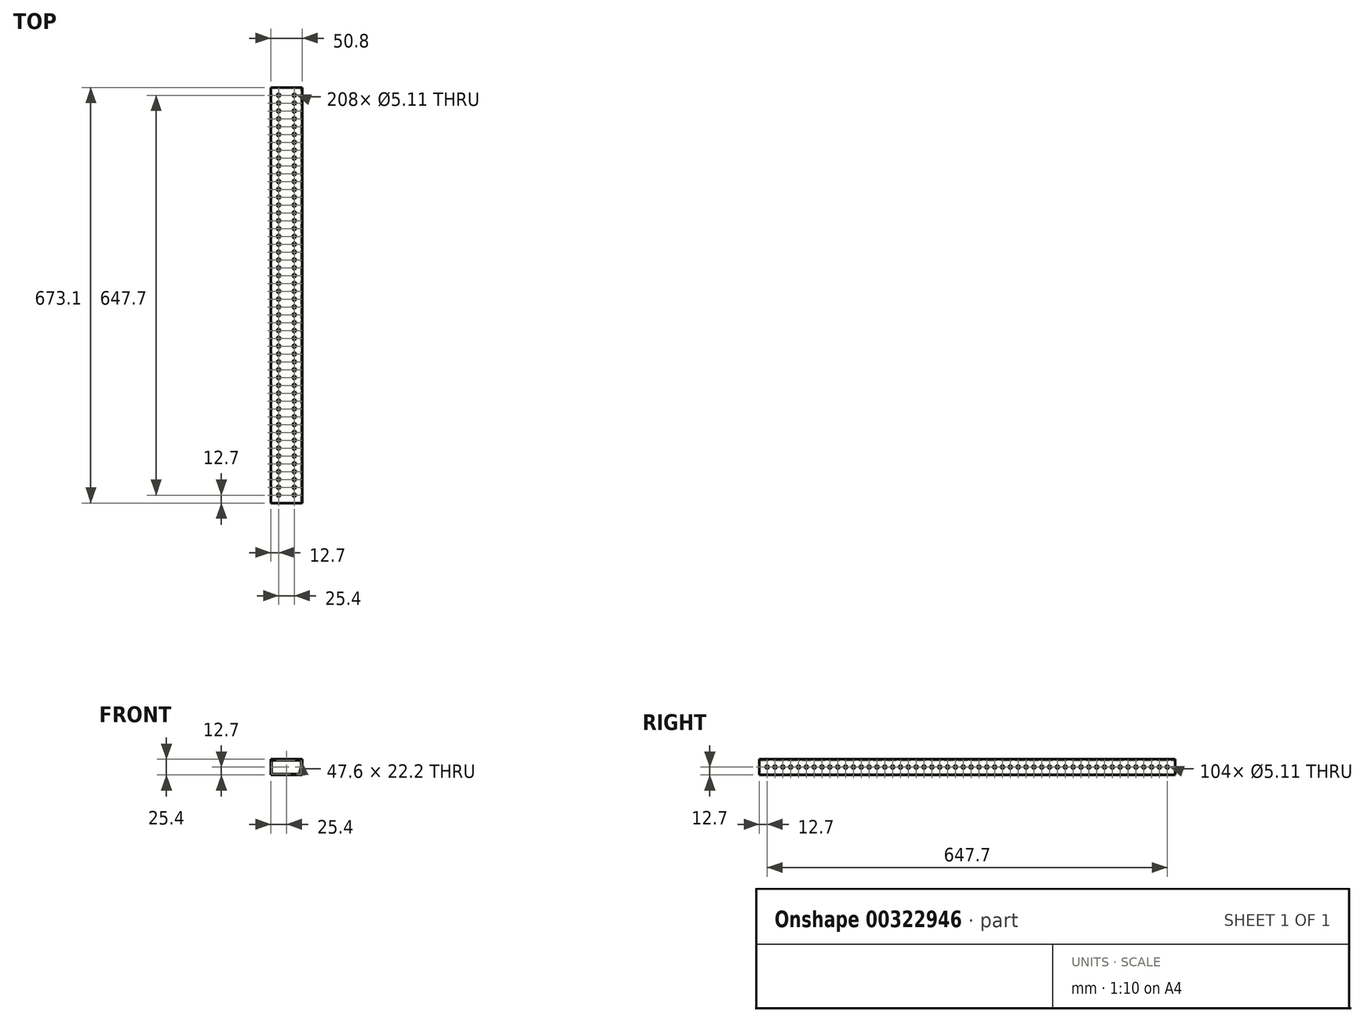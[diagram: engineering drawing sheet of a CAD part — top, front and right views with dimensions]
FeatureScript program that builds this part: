
annotation { "Feature Type Name" : "Feature", "Feature Type Description" : "" }
export const myFeature = defineFeature(function(context is Context, id is Id, definition is map)
    precondition{}
    {
        {
            var Q0;
            Q0=qCreatedBy(makeId("Front.planeOp"),FACE);
            var sketch = newSketch(context, id + "F0", { "sketchPlane" : qUnion([Q0])});
            skLineSegment(sketch, "E0.bottom", {"start": v(-25.4, 12.7) * mm, "end": v(25.4, 12.7) * mm});
            skLineSegment(sketch, "E0.top", {"start": v(-25.4, -12.7) * mm, "end": v(25.4, -12.7) * mm});
            skLineSegment(sketch, "E0.left", {"start": v(-25.4, 12.7) * mm, "end": v(-25.4, -12.7) * mm});
            skLineSegment(sketch, "E0.right", {"start": v(25.4, 12.7) * mm, "end": v(25.4, -12.7) * mm});
            skPoint(sketch, "E0.middle", {"position": v(0, 0) * mm});
            skLineSegment(sketch, "E1.bottom", {"start": v(-23.8, 11.1) * mm, "end": v(23.8, 11.1) * mm});
            skLineSegment(sketch, "E1.top", {"start": v(-23.8, -11.1) * mm, "end": v(23.8, -11.1) * mm});
            skLineSegment(sketch, "E1.left", {"start": v(-23.8, 11.1) * mm, "end": v(-23.8, -11.1) * mm});
            skLineSegment(sketch, "E1.right", {"start": v(23.8, 11.1) * mm, "end": v(23.8, -11.1) * mm});
            skSolve(sketch);
        }
        {
            var Q0;
            Q0=makeQuery(id+"F0.imprint","IMPRINT",FACE,{"disambiguationData":[TD([[makeQuery(id+"F0.imprint","IMPRINT",EDGE,{"derivedFrom":sQuery(id+"F0.wireOp",EDGE,"E0.bottom")}),-1.0]])]});
            extrude(context, id + "F1", {"entities" : qUnion([Q0]), "depth" : 673.1 * mm});
        }
        {
            var Q0;
            Q0=makeQuery(id+"F1.opExtrude","SWEPT_FACE",FACE,{"disambiguationData":[OSD([sQuery(id+"F0.wireOp",EDGE,"E0.bottom")])]});
            var sketch = newSketch(context, id + "F2", { "sketchPlane" : qUnion([Q0])});
            skCircle(sketch, "E2", {"center": v(-12.7, -660.4) * mm, "radius": 2.55 * mm});
            skCircle(sketch, "E3.0.1.0", {"center": v(-12.7, -647.7) * mm, "radius": 2.55 * mm});
            skCircle(sketch, "E3.0.2.0", {"center": v(-12.7, -635) * mm, "radius": 2.55 * mm});
            skCircle(sketch, "E3.0.3.0", {"center": v(-12.7, -622.3) * mm, "radius": 2.55 * mm});
            skCircle(sketch, "E3.0.4.0", {"center": v(-12.7, -609.6) * mm, "radius": 2.55 * mm});
            skCircle(sketch, "E3.0.5.0", {"center": v(-12.7, -596.9) * mm, "radius": 2.55 * mm});
            skCircle(sketch, "E3.0.6.0", {"center": v(-12.7, -584.2) * mm, "radius": 2.55 * mm});
            skCircle(sketch, "E3.0.7.0", {"center": v(-12.7, -571.5) * mm, "radius": 2.55 * mm});
            skCircle(sketch, "E3.0.8.0", {"center": v(-12.7, -558.8) * mm, "radius": 2.55 * mm});
            skCircle(sketch, "E3.0.9.0", {"center": v(-12.7, -546.1) * mm, "radius": 2.55 * mm});
            skCircle(sketch, "E3.0.10.0", {"center": v(-12.7, -533.4) * mm, "radius": 2.55 * mm});
            skCircle(sketch, "E3.0.11.0", {"center": v(-12.7, -520.7) * mm, "radius": 2.55 * mm});
            skCircle(sketch, "E3.0.12.0", {"center": v(-12.7, -508) * mm, "radius": 2.55 * mm});
            skCircle(sketch, "E3.0.13.0", {"center": v(-12.7, -495.3) * mm, "radius": 2.55 * mm});
            skCircle(sketch, "E3.0.14.0", {"center": v(-12.7, -482.6) * mm, "radius": 2.55 * mm});
            skCircle(sketch, "E3.0.15.0", {"center": v(-12.7, -469.9) * mm, "radius": 2.55 * mm});
            skCircle(sketch, "E3.0.16.0", {"center": v(-12.7, -457.2) * mm, "radius": 2.55 * mm});
            skCircle(sketch, "E3.0.17.0", {"center": v(-12.7, -444.5) * mm, "radius": 2.55 * mm});
            skCircle(sketch, "E3.0.18.0", {"center": v(-12.7, -431.8) * mm, "radius": 2.55 * mm});
            skCircle(sketch, "E3.0.19.0", {"center": v(-12.7, -419.1) * mm, "radius": 2.55 * mm});
            skCircle(sketch, "E3.0.20.0", {"center": v(-12.7, -406.4) * mm, "radius": 2.55 * mm});
            skCircle(sketch, "E3.0.21.0", {"center": v(-12.7, -393.7) * mm, "radius": 2.55 * mm});
            skCircle(sketch, "E3.0.22.0", {"center": v(-12.7, -381) * mm, "radius": 2.55 * mm});
            skCircle(sketch, "E3.0.23.0", {"center": v(-12.7, -368.3) * mm, "radius": 2.55 * mm});
            skCircle(sketch, "E3.0.24.0", {"center": v(-12.7, -355.6) * mm, "radius": 2.55 * mm});
            skCircle(sketch, "E3.0.25.0", {"center": v(-12.7, -342.9) * mm, "radius": 2.55 * mm});
            skCircle(sketch, "E3.1.0.0", {"center": v(12.7, -660.4) * mm, "radius": 2.55 * mm});
            skCircle(sketch, "E3.1.1.0", {"center": v(12.7, -647.7) * mm, "radius": 2.55 * mm});
            skCircle(sketch, "E3.1.2.0", {"center": v(12.7, -635) * mm, "radius": 2.55 * mm});
            skCircle(sketch, "E3.1.3.0", {"center": v(12.7, -622.3) * mm, "radius": 2.55 * mm});
            skCircle(sketch, "E3.1.4.0", {"center": v(12.7, -609.6) * mm, "radius": 2.55 * mm});
            skCircle(sketch, "E3.1.5.0", {"center": v(12.7, -596.9) * mm, "radius": 2.55 * mm});
            skCircle(sketch, "E3.1.6.0", {"center": v(12.7, -584.2) * mm, "radius": 2.55 * mm});
            skCircle(sketch, "E3.1.7.0", {"center": v(12.7, -571.5) * mm, "radius": 2.55 * mm});
            skCircle(sketch, "E3.1.8.0", {"center": v(12.7, -558.8) * mm, "radius": 2.55 * mm});
            skCircle(sketch, "E3.1.9.0", {"center": v(12.7, -546.1) * mm, "radius": 2.55 * mm});
            skCircle(sketch, "E3.1.10.0", {"center": v(12.7, -533.4) * mm, "radius": 2.55 * mm});
            skCircle(sketch, "E3.1.11.0", {"center": v(12.7, -520.7) * mm, "radius": 2.55 * mm});
            skCircle(sketch, "E3.1.12.0", {"center": v(12.7, -508) * mm, "radius": 2.55 * mm});
            skCircle(sketch, "E3.1.13.0", {"center": v(12.7, -495.3) * mm, "radius": 2.55 * mm});
            skCircle(sketch, "E3.1.14.0", {"center": v(12.7, -482.6) * mm, "radius": 2.55 * mm});
            skCircle(sketch, "E3.1.15.0", {"center": v(12.7, -469.9) * mm, "radius": 2.55 * mm});
            skCircle(sketch, "E3.1.16.0", {"center": v(12.7, -457.2) * mm, "radius": 2.55 * mm});
            skCircle(sketch, "E3.1.17.0", {"center": v(12.7, -444.5) * mm, "radius": 2.55 * mm});
            skCircle(sketch, "E3.1.18.0", {"center": v(12.7, -431.8) * mm, "radius": 2.55 * mm});
            skCircle(sketch, "E3.1.19.0", {"center": v(12.7, -419.1) * mm, "radius": 2.55 * mm});
            skCircle(sketch, "E3.1.20.0", {"center": v(12.7, -406.4) * mm, "radius": 2.55 * mm});
            skCircle(sketch, "E3.1.21.0", {"center": v(12.7, -393.7) * mm, "radius": 2.55 * mm});
            skCircle(sketch, "E3.1.22.0", {"center": v(12.7, -381) * mm, "radius": 2.55 * mm});
            skCircle(sketch, "E3.1.23.0", {"center": v(12.7, -368.3) * mm, "radius": 2.55 * mm});
            skCircle(sketch, "E3.1.24.0", {"center": v(12.7, -355.6) * mm, "radius": 2.55 * mm});
            skCircle(sketch, "E3.1.25.0", {"center": v(12.7, -342.9) * mm, "radius": 2.55 * mm});
            skLineSegment(sketch, "E3.direction1", {"start": v(-12.7, -660.4) * mm, "end": v(12.7, -660.4) * mm, "construction": true});
            skLineSegment(sketch, "E3.direction2", {"start": v(-12.7, -660.4) * mm, "end": v(-12.7, -647.7) * mm, "construction": true});
            skCircle(sketch, "E4.0.0.26", {"center": v(-12.7, -330.2) * mm, "radius": 2.55 * mm});
            skCircle(sketch, "E4.0.0.27", {"center": v(-12.7, -317.5) * mm, "radius": 2.55 * mm});
            skCircle(sketch, "E4.0.0.28", {"center": v(-12.7, -304.8) * mm, "radius": 2.55 * mm});
            skCircle(sketch, "E4.0.0.29", {"center": v(-12.7, -292.1) * mm, "radius": 2.55 * mm});
            skCircle(sketch, "E4.0.0.30", {"center": v(-12.7, -279.4) * mm, "radius": 2.55 * mm});
            skCircle(sketch, "E4.0.0.31", {"center": v(-12.7, -266.7) * mm, "radius": 2.55 * mm});
            skCircle(sketch, "E4.0.0.32", {"center": v(-12.7, -254) * mm, "radius": 2.55 * mm});
            skCircle(sketch, "E4.0.0.33", {"center": v(-12.7, -241.3) * mm, "radius": 2.55 * mm});
            skCircle(sketch, "E4.0.0.34", {"center": v(-12.7, -228.6) * mm, "radius": 2.55 * mm});
            skCircle(sketch, "E4.0.0.35", {"center": v(-12.7, -215.9) * mm, "radius": 2.55 * mm});
            skCircle(sketch, "E4.0.0.36", {"center": v(-12.7, -203.2) * mm, "radius": 2.55 * mm});
            skCircle(sketch, "E4.0.0.37", {"center": v(-12.7, -190.5) * mm, "radius": 2.55 * mm});
            skCircle(sketch, "E4.0.0.38", {"center": v(-12.7, -177.8) * mm, "radius": 2.55 * mm});
            skCircle(sketch, "E4.0.0.39", {"center": v(-12.7, -165.1) * mm, "radius": 2.55 * mm});
            skCircle(sketch, "E4.0.0.40", {"center": v(-12.7, -152.4) * mm, "radius": 2.55 * mm});
            skCircle(sketch, "E4.0.0.41", {"center": v(-12.7, -139.7) * mm, "radius": 2.55 * mm});
            skCircle(sketch, "E4.0.0.42", {"center": v(-12.7, -127) * mm, "radius": 2.55 * mm});
            skCircle(sketch, "E4.0.0.43", {"center": v(-12.7, -114.3) * mm, "radius": 2.55 * mm});
            skCircle(sketch, "E4.0.0.44", {"center": v(-12.7, -101.6) * mm, "radius": 2.55 * mm});
            skCircle(sketch, "E4.0.0.45", {"center": v(-12.7, -88.9) * mm, "radius": 2.55 * mm});
            skCircle(sketch, "E4.0.1.26", {"center": v(12.7, -330.2) * mm, "radius": 2.55 * mm});
            skCircle(sketch, "E4.0.1.27", {"center": v(12.7, -317.5) * mm, "radius": 2.55 * mm});
            skCircle(sketch, "E4.0.1.28", {"center": v(12.7, -304.8) * mm, "radius": 2.55 * mm});
            skCircle(sketch, "E4.0.1.29", {"center": v(12.7, -292.1) * mm, "radius": 2.55 * mm});
            skCircle(sketch, "E4.0.1.30", {"center": v(12.7, -279.4) * mm, "radius": 2.55 * mm});
            skCircle(sketch, "E4.0.1.31", {"center": v(12.7, -266.7) * mm, "radius": 2.55 * mm});
            skCircle(sketch, "E4.0.1.32", {"center": v(12.7, -254) * mm, "radius": 2.55 * mm});
            skCircle(sketch, "E4.0.1.33", {"center": v(12.7, -241.3) * mm, "radius": 2.55 * mm});
            skCircle(sketch, "E4.0.1.34", {"center": v(12.7, -228.6) * mm, "radius": 2.55 * mm});
            skCircle(sketch, "E4.0.1.35", {"center": v(12.7, -215.9) * mm, "radius": 2.55 * mm});
            skCircle(sketch, "E4.0.1.36", {"center": v(12.7, -203.2) * mm, "radius": 2.55 * mm});
            skCircle(sketch, "E4.0.1.37", {"center": v(12.7, -190.5) * mm, "radius": 2.55 * mm});
            skCircle(sketch, "E4.0.1.38", {"center": v(12.7, -177.8) * mm, "radius": 2.55 * mm});
            skCircle(sketch, "E4.0.1.39", {"center": v(12.7, -165.1) * mm, "radius": 2.55 * mm});
            skCircle(sketch, "E4.0.1.40", {"center": v(12.7, -152.4) * mm, "radius": 2.55 * mm});
            skCircle(sketch, "E4.0.1.41", {"center": v(12.7, -139.7) * mm, "radius": 2.55 * mm});
            skCircle(sketch, "E4.0.1.42", {"center": v(12.7, -127) * mm, "radius": 2.55 * mm});
            skCircle(sketch, "E4.0.1.43", {"center": v(12.7, -114.3) * mm, "radius": 2.55 * mm});
            skCircle(sketch, "E4.0.1.44", {"center": v(12.7, -101.6) * mm, "radius": 2.55 * mm});
            skCircle(sketch, "E4.0.1.45", {"center": v(12.7, -88.9) * mm, "radius": 2.55 * mm});
            skCircle(sketch, "E5.0.0.46", {"center": v(-12.7, -76.2) * mm, "radius": 2.55 * mm});
            skCircle(sketch, "E5.0.0.47", {"center": v(-12.7, -63.5) * mm, "radius": 2.55 * mm});
            skCircle(sketch, "E5.0.0.48", {"center": v(-12.7, -50.8) * mm, "radius": 2.55 * mm});
            skCircle(sketch, "E5.0.0.49", {"center": v(-12.7, -38.1) * mm, "radius": 2.55 * mm});
            skCircle(sketch, "E5.0.1.46", {"center": v(12.7, -76.2) * mm, "radius": 2.55 * mm});
            skCircle(sketch, "E5.0.1.47", {"center": v(12.7, -63.5) * mm, "radius": 2.55 * mm});
            skCircle(sketch, "E5.0.1.48", {"center": v(12.7, -50.8) * mm, "radius": 2.55 * mm});
            skCircle(sketch, "E5.0.1.49", {"center": v(12.7, -38.1) * mm, "radius": 2.55 * mm});
            skCircle(sketch, "E6.0.0.50", {"center": v(-12.7, -25.4) * mm, "radius": 2.55 * mm});
            skCircle(sketch, "E6.0.1.50", {"center": v(12.7, -25.4) * mm, "radius": 2.55 * mm});
            skCircle(sketch, "E7.0.0.51", {"center": v(-12.7, -12.7) * mm, "radius": 2.55 * mm});
            skCircle(sketch, "E7.0.1.51", {"center": v(12.7, -12.7) * mm, "radius": 2.55 * mm});
            skSolve(sketch);
        }
        {
            var Q0;
            Q0=makeQuery(id+"F1.opExtrude","SWEPT_FACE",FACE,{"disambiguationData":[OSD([sQuery(id+"F0.wireOp",EDGE,"E0.right")])]});
            var sketch = newSketch(context, id + "F3", { "sketchPlane" : qUnion([Q0])});
            skCircle(sketch, "E8", {"center": v(-660.4, 0) * mm, "radius": 2.55 * mm});
            skCircle(sketch, "E9.1.0.0", {"center": v(-647.7, 0) * mm, "radius": 2.55 * mm});
            skCircle(sketch, "E9.2.0.0", {"center": v(-635, 0) * mm, "radius": 2.55 * mm});
            skCircle(sketch, "E9.3.0.0", {"center": v(-622.3, 0) * mm, "radius": 2.55 * mm});
            skCircle(sketch, "E9.4.0.0", {"center": v(-609.6, 0) * mm, "radius": 2.55 * mm});
            skCircle(sketch, "E9.5.0.0", {"center": v(-596.9, 0) * mm, "radius": 2.55 * mm});
            skCircle(sketch, "E9.6.0.0", {"center": v(-584.2, 0) * mm, "radius": 2.55 * mm});
            skCircle(sketch, "E9.7.0.0", {"center": v(-571.5, 0) * mm, "radius": 2.55 * mm});
            skCircle(sketch, "E9.8.0.0", {"center": v(-558.8, 0) * mm, "radius": 2.55 * mm});
            skCircle(sketch, "E9.9.0.0", {"center": v(-546.1, 0) * mm, "radius": 2.55 * mm});
            skCircle(sketch, "E9.10.0.0", {"center": v(-533.4, 0) * mm, "radius": 2.55 * mm});
            skCircle(sketch, "E9.11.0.0", {"center": v(-520.7, 0) * mm, "radius": 2.55 * mm});
            skCircle(sketch, "E9.12.0.0", {"center": v(-508, 0) * mm, "radius": 2.55 * mm});
            skCircle(sketch, "E9.13.0.0", {"center": v(-495.3, 0) * mm, "radius": 2.55 * mm});
            skCircle(sketch, "E9.14.0.0", {"center": v(-482.6, 0) * mm, "radius": 2.55 * mm});
            skCircle(sketch, "E9.15.0.0", {"center": v(-469.9, 0) * mm, "radius": 2.55 * mm});
            skCircle(sketch, "E9.16.0.0", {"center": v(-457.2, 0) * mm, "radius": 2.55 * mm});
            skCircle(sketch, "E9.17.0.0", {"center": v(-444.5, 0) * mm, "radius": 2.55 * mm});
            skCircle(sketch, "E9.18.0.0", {"center": v(-431.8, 0) * mm, "radius": 2.55 * mm});
            skCircle(sketch, "E9.19.0.0", {"center": v(-419.1, 0) * mm, "radius": 2.55 * mm});
            skCircle(sketch, "E9.20.0.0", {"center": v(-406.4, 0) * mm, "radius": 2.55 * mm});
            skCircle(sketch, "E9.21.0.0", {"center": v(-393.7, 0) * mm, "radius": 2.55 * mm});
            skCircle(sketch, "E9.22.0.0", {"center": v(-381, 0) * mm, "radius": 2.55 * mm});
            skCircle(sketch, "E9.23.0.0", {"center": v(-368.3, 0) * mm, "radius": 2.55 * mm});
            skCircle(sketch, "E9.24.0.0", {"center": v(-355.6, 0) * mm, "radius": 2.55 * mm});
            skCircle(sketch, "E9.25.0.0", {"center": v(-342.9, 0) * mm, "radius": 2.55 * mm});
            skLineSegment(sketch, "E9.direction1", {"start": v(-660.4, 0) * mm, "end": v(-647.7, 0) * mm, "construction": true});
            skCircle(sketch, "E10.0.26.0", {"center": v(-330.2, 0) * mm, "radius": 2.55 * mm});
            skCircle(sketch, "E10.0.27.0", {"center": v(-317.5, 0) * mm, "radius": 2.55 * mm});
            skCircle(sketch, "E10.0.28.0", {"center": v(-304.8, 0) * mm, "radius": 2.55 * mm});
            skCircle(sketch, "E10.0.29.0", {"center": v(-292.1, 0) * mm, "radius": 2.55 * mm});
            skCircle(sketch, "E10.0.30.0", {"center": v(-279.4, 0) * mm, "radius": 2.55 * mm});
            skCircle(sketch, "E10.0.31.0", {"center": v(-266.7, 0) * mm, "radius": 2.55 * mm});
            skCircle(sketch, "E10.0.32.0", {"center": v(-254, 0) * mm, "radius": 2.55 * mm});
            skCircle(sketch, "E10.0.33.0", {"center": v(-241.3, 0) * mm, "radius": 2.55 * mm});
            skCircle(sketch, "E10.0.34.0", {"center": v(-228.6, 0) * mm, "radius": 2.55 * mm});
            skCircle(sketch, "E10.0.35.0", {"center": v(-215.9, 0) * mm, "radius": 2.55 * mm});
            skCircle(sketch, "E10.0.36.0", {"center": v(-203.2, 0) * mm, "radius": 2.55 * mm});
            skCircle(sketch, "E10.0.37.0", {"center": v(-190.5, 0) * mm, "radius": 2.55 * mm});
            skCircle(sketch, "E10.0.38.0", {"center": v(-177.8, 0) * mm, "radius": 2.55 * mm});
            skCircle(sketch, "E10.0.39.0", {"center": v(-165.1, 0) * mm, "radius": 2.55 * mm});
            skCircle(sketch, "E10.0.40.0", {"center": v(-152.4, 0) * mm, "radius": 2.55 * mm});
            skCircle(sketch, "E10.0.41.0", {"center": v(-139.7, 0) * mm, "radius": 2.55 * mm});
            skCircle(sketch, "E10.0.42.0", {"center": v(-127, 0) * mm, "radius": 2.55 * mm});
            skCircle(sketch, "E10.0.43.0", {"center": v(-114.3, 0) * mm, "radius": 2.55 * mm});
            skCircle(sketch, "E10.0.44.0", {"center": v(-101.6, 0) * mm, "radius": 2.55 * mm});
            skCircle(sketch, "E10.0.45.0", {"center": v(-88.9, 0) * mm, "radius": 2.55 * mm});
            skCircle(sketch, "E10.0.46.0", {"center": v(-76.2, 0) * mm, "radius": 2.55 * mm});
            skCircle(sketch, "E10.0.47.0", {"center": v(-63.5, 0) * mm, "radius": 2.55 * mm});
            skCircle(sketch, "E10.0.48.0", {"center": v(-50.8, 0) * mm, "radius": 2.55 * mm});
            skCircle(sketch, "E10.0.49.0", {"center": v(-38.1, 0) * mm, "radius": 2.55 * mm});
            skCircle(sketch, "E10.0.50.0", {"center": v(-25.4, 0) * mm, "radius": 2.55 * mm});
            skCircle(sketch, "E10.0.51.0", {"center": v(-12.7, 0) * mm, "radius": 2.55 * mm});
            skSolve(sketch);
        }
        {
            var Q0;
            Q0=sQuery(id+"F3.wireOp",VERTEX,"E9.25.0.0.center");
            var Q1;
            Q1=sQuery(id+"F3.wireOp",VERTEX,"E9.23.0.0.center");
            var Q2;
            Q2=sQuery(id+"F3.wireOp",VERTEX,"E9.16.0.0.center");
            var Q3;
            Q3=sQuery(id+"F3.wireOp",VERTEX,"E9.14.0.0.center");
            var Q4;
            Q4=sQuery(id+"F3.wireOp",VERTEX,"E9.20.0.0.center");
            var Q5;
            Q5=sQuery(id+"F3.wireOp",VERTEX,"E9.18.0.0.center");
            var Q6;
            Q6=sQuery(id+"F3.wireOp",VERTEX,"E8.center");
            var Q7;
            Q7=sQuery(id+"F3.wireOp",VERTEX,"E9.3.0.0.center");
            var Q8;
            Q8=sQuery(id+"F3.wireOp",VERTEX,"E9.2.0.0.center");
            var Q9;
            Q9=sQuery(id+"F3.wireOp",VERTEX,"E9.4.0.0.center");
            var Q10;
            Q10=sQuery(id+"F3.wireOp",VERTEX,"E9.5.0.0.center");
            var Q11;
            Q11=sQuery(id+"F3.wireOp",VERTEX,"E9.12.0.0.center");
            var Q12;
            Q12=sQuery(id+"F3.wireOp",VERTEX,"E9.11.0.0.center");
            var Q13;
            Q13=sQuery(id+"F3.wireOp",VERTEX,"E9.21.0.0.center");
            var Q14;
            Q14=sQuery(id+"F3.wireOp",VERTEX,"E9.13.0.0.center");
            var Q15;
            Q15=sQuery(id+"F3.wireOp",VERTEX,"E9.direction1.end");
            var Q16;
            Q16=sQuery(id+"F3.wireOp",VERTEX,"E9.24.0.0.center");
            var Q17;
            Q17=sQuery(id+"F3.wireOp",VERTEX,"E9.15.0.0.center");
            var Q18;
            Q18=sQuery(id+"F3.wireOp",VERTEX,"E9.7.0.0.center");
            var Q19;
            Q19=sQuery(id+"F3.wireOp",VERTEX,"E9.19.0.0.center");
            var Q20;
            Q20=sQuery(id+"F3.wireOp",VERTEX,"E9.6.0.0.center");
            var Q21;
            Q21=sQuery(id+"F3.wireOp",VERTEX,"E9.9.0.0.center");
            var Q22;
            Q22=sQuery(id+"F3.wireOp",VERTEX,"E9.17.0.0.center");
            var Q23;
            Q23=sQuery(id+"F3.wireOp",VERTEX,"E9.8.0.0.center");
            var Q24;
            Q24=sQuery(id+"F3.wireOp",VERTEX,"E9.10.0.0.center");
            var Q25;
            Q25=sQuery(id+"F3.wireOp",VERTEX,"E9.22.0.0.center");
            var Q26;
            Q26=sQuery(id+"F3.wireOp",VERTEX,"E10.0.48.0.center");
            var Q27;
            Q27=sQuery(id+"F3.wireOp",VERTEX,"E10.0.31.0.center");
            var Q28;
            Q28=sQuery(id+"F3.wireOp",VERTEX,"E10.0.32.0.center");
            var Q29;
            Q29=sQuery(id+"F3.wireOp",VERTEX,"E10.0.44.0.center");
            var Q30;
            Q30=sQuery(id+"F3.wireOp",VERTEX,"E10.0.36.0.center");
            var Q31;
            Q31=sQuery(id+"F3.wireOp",VERTEX,"E10.0.28.0.center");
            var Q32;
            Q32=sQuery(id+"F3.wireOp",VERTEX,"E10.0.27.0.center");
            var Q33;
            Q33=sQuery(id+"F3.wireOp",VERTEX,"E10.0.43.0.center");
            var Q34;
            Q34=sQuery(id+"F3.wireOp",VERTEX,"E10.0.51.0.center");
            var Q35;
            Q35=sQuery(id+"F3.wireOp",VERTEX,"E10.0.29.0.center");
            var Q36;
            Q36=sQuery(id+"F3.wireOp",VERTEX,"E10.0.33.0.center");
            var Q37;
            Q37=sQuery(id+"F3.wireOp",VERTEX,"E10.0.37.0.center");
            var Q38;
            Q38=sQuery(id+"F3.wireOp",VERTEX,"E10.0.49.0.center");
            var Q39;
            Q39=sQuery(id+"F3.wireOp",VERTEX,"E10.0.45.0.center");
            var Q40;
            Q40=sQuery(id+"F3.wireOp",VERTEX,"E10.0.39.0.center");
            var Q41;
            Q41=sQuery(id+"F3.wireOp",VERTEX,"E10.0.46.0.center");
            var Q42;
            Q42=sQuery(id+"F3.wireOp",VERTEX,"E10.0.30.0.center");
            var Q43;
            Q43=sQuery(id+"F3.wireOp",VERTEX,"E10.0.50.0.center");
            var Q44;
            Q44=sQuery(id+"F3.wireOp",VERTEX,"E10.0.40.0.center");
            var Q45;
            Q45=sQuery(id+"F3.wireOp",VERTEX,"E10.0.34.0.center");
            var Q46;
            Q46=sQuery(id+"F3.wireOp",VERTEX,"E10.0.35.0.center");
            var Q47;
            Q47=sQuery(id+"F3.wireOp",VERTEX,"E10.0.41.0.center");
            var Q48;
            Q48=sQuery(id+"F3.wireOp",VERTEX,"E10.0.38.0.center");
            var Q49;
            Q49=sQuery(id+"F3.wireOp",VERTEX,"E10.0.47.0.center");
            var Q50;
            Q50=sQuery(id+"F3.wireOp",VERTEX,"E10.0.42.0.center");
            var Q51;
            Q51=sQuery(id+"F3.wireOp",VERTEX,"E10.0.26.0.center");
            var Q52;
            Q52=makeQuery(id+"F1.opExtrude","SWEPT_BODY",BODY,{"disambiguationData":[OSD([sQuery(id+"F0.wireOp",EDGE,"E0.bottom"),sQuery(id+"F0.wireOp",EDGE,"E0.top"),sQuery(id+"F0.wireOp",EDGE,"E0.left"),sQuery(id+"F0.wireOp",EDGE,"E0.right"),sQuery(id+"F0.wireOp",EDGE,"E1.bottom"),sQuery(id+"F0.wireOp",EDGE,"E1.top"),sQuery(id+"F0.wireOp",EDGE,"E1.left"),sQuery(id+"F0.wireOp",EDGE,"E1.right")])]});
            hole(context, id + "F4", {"style" : HoleStyle.SIMPLE, "endStyle" : HoleEndStyle.THROUGH, "holeDiameter" : 5.1 * mm, "isTappedThrough" : true, "tappedDepth" : 12.7 * mm, "tapClearance" : 3, "locations" : qUnion([Q0, Q1, Q2, Q3, Q4, Q5, Q6, Q7, Q8, Q9, Q10, Q11, Q12, Q13, Q14, Q15, Q16, Q17, Q18, Q19, Q20, Q21, Q22, Q23, Q24, Q25, Q26, Q27, Q28, Q29, Q30, Q31, Q32, Q33, Q34, Q35, Q36, Q37, Q38, Q39, Q40, Q41, Q42, Q43, Q44, Q45, Q46, Q47, Q48, Q49, Q50, Q51]), "scope" : qUnion([Q52])});
        }
        {
            var Q0;
            Q0=sQuery(id+"F2.wireOp",VERTEX,"E4.0.0.39.center");
            var Q1;
            Q1=sQuery(id+"F2.wireOp",VERTEX,"E4.0.0.32.center");
            var Q2;
            Q2=sQuery(id+"F2.wireOp",VERTEX,"E3.0.23.0.center");
            var Q3;
            Q3=sQuery(id+"F2.wireOp",VERTEX,"E4.0.0.29.center");
            var Q4;
            Q4=sQuery(id+"F2.wireOp",VERTEX,"E3.1.22.0.center");
            var Q5;
            Q5=sQuery(id+"F2.wireOp",VERTEX,"E4.0.0.31.center");
            var Q6;
            Q6=sQuery(id+"F2.wireOp",VERTEX,"E3.1.23.0.center");
            var Q7;
            Q7=sQuery(id+"F2.wireOp",VERTEX,"E4.0.1.44.center");
            var Q8;
            Q8=sQuery(id+"F2.wireOp",VERTEX,"E5.0.1.46.center");
            var Q9;
            Q9=sQuery(id+"F2.wireOp",VERTEX,"E4.0.1.34.center");
            var Q10;
            Q10=sQuery(id+"F2.wireOp",VERTEX,"E4.0.0.44.center");
            var Q11;
            Q11=sQuery(id+"F2.wireOp",VERTEX,"E3.0.25.0.center");
            var Q12;
            Q12=sQuery(id+"F2.wireOp",VERTEX,"E4.0.1.43.center");
            var Q13;
            Q13=sQuery(id+"F2.wireOp",VERTEX,"E4.0.1.40.center");
            var Q14;
            Q14=sQuery(id+"F2.wireOp",VERTEX,"E4.0.1.35.center");
            var Q15;
            Q15=sQuery(id+"F2.wireOp",VERTEX,"E4.0.0.45.center");
            var Q16;
            Q16=sQuery(id+"F2.wireOp",VERTEX,"E4.0.1.41.center");
            var Q17;
            Q17=sQuery(id+"F2.wireOp",VERTEX,"E5.0.1.47.center");
            var Q18;
            Q18=sQuery(id+"F2.wireOp",VERTEX,"E4.0.0.38.center");
            var Q19;
            Q19=sQuery(id+"F2.wireOp",VERTEX,"E4.0.1.27.center");
            var Q20;
            Q20=sQuery(id+"F2.wireOp",VERTEX,"E4.0.1.28.center");
            var Q21;
            Q21=sQuery(id+"F2.wireOp",VERTEX,"E4.0.1.33.center");
            var Q22;
            Q22=sQuery(id+"F2.wireOp",VERTEX,"E4.0.1.32.center");
            var Q23;
            Q23=sQuery(id+"F2.wireOp",VERTEX,"E4.0.1.42.center");
            var Q24;
            Q24=sQuery(id+"F2.wireOp",VERTEX,"E5.0.0.46.center");
            var Q25;
            Q25=sQuery(id+"F2.wireOp",VERTEX,"E4.0.1.38.center");
            var Q26;
            Q26=sQuery(id+"F2.wireOp",VERTEX,"E4.0.1.29.center");
            var Q27;
            Q27=sQuery(id+"F2.wireOp",VERTEX,"E4.0.0.43.center");
            var Q28;
            Q28=sQuery(id+"F2.wireOp",VERTEX,"E4.0.1.39.center");
            var Q29;
            Q29=sQuery(id+"F2.wireOp",VERTEX,"E4.0.0.33.center");
            var Q30;
            Q30=sQuery(id+"F2.wireOp",VERTEX,"E4.0.0.27.center");
            var Q31;
            Q31=sQuery(id+"F2.wireOp",VERTEX,"E3.1.20.0.center");
            var Q32;
            Q32=sQuery(id+"F2.wireOp",VERTEX,"E3.1.19.0.center");
            var Q33;
            Q33=sQuery(id+"F2.wireOp",VERTEX,"E4.0.0.35.center");
            var Q34;
            Q34=sQuery(id+"F2.wireOp",VERTEX,"E4.0.1.37.center");
            var Q35;
            Q35=sQuery(id+"F2.wireOp",VERTEX,"E4.0.1.30.center");
            var Q36;
            Q36=sQuery(id+"F2.wireOp",VERTEX,"E4.0.0.34.center");
            var Q37;
            Q37=sQuery(id+"F2.wireOp",VERTEX,"E3.1.18.0.center");
            var Q38;
            Q38=sQuery(id+"F2.wireOp",VERTEX,"E3.1.25.0.center");
            var Q39;
            Q39=sQuery(id+"F2.wireOp",VERTEX,"E4.0.0.28.center");
            var Q40;
            Q40=sQuery(id+"F2.wireOp",VERTEX,"E3.1.21.0.center");
            var Q41;
            Q41=sQuery(id+"F2.wireOp",VERTEX,"E4.0.0.30.center");
            var Q42;
            Q42=sQuery(id+"F2.wireOp",VERTEX,"E3.0.21.0.center");
            var Q43;
            Q43=sQuery(id+"F2.wireOp",VERTEX,"E3.0.20.0.center");
            var Q44;
            Q44=sQuery(id+"F2.wireOp",VERTEX,"E3.0.24.0.center");
            var Q45;
            Q45=sQuery(id+"F2.wireOp",VERTEX,"E4.0.1.26.center");
            var Q46;
            Q46=sQuery(id+"F2.wireOp",VERTEX,"E3.0.18.0.center");
            var Q47;
            Q47=sQuery(id+"F2.wireOp",VERTEX,"E3.0.22.0.center");
            var Q48;
            Q48=sQuery(id+"F2.wireOp",VERTEX,"E4.0.1.36.center");
            var Q49;
            Q49=sQuery(id+"F2.wireOp",VERTEX,"E5.0.0.49.center");
            var Q50;
            Q50=sQuery(id+"F2.wireOp",VERTEX,"E4.0.0.37.center");
            var Q51;
            Q51=sQuery(id+"F2.wireOp",VERTEX,"E4.0.0.40.center");
            var Q52;
            Q52=sQuery(id+"F2.wireOp",VERTEX,"E3.1.24.0.center");
            var Q53;
            Q53=sQuery(id+"F2.wireOp",VERTEX,"E4.0.1.45.center");
            var Q54;
            Q54=sQuery(id+"F2.wireOp",VERTEX,"E4.0.0.26.center");
            var Q55;
            Q55=sQuery(id+"F2.wireOp",VERTEX,"E5.0.0.47.center");
            var Q56;
            Q56=sQuery(id+"F2.wireOp",VERTEX,"E5.0.1.48.center");
            var Q57;
            Q57=sQuery(id+"F2.wireOp",VERTEX,"E5.0.0.48.center");
            var Q58;
            Q58=sQuery(id+"F2.wireOp",VERTEX,"E4.0.0.36.center");
            var Q59;
            Q59=sQuery(id+"F2.wireOp",VERTEX,"E4.0.1.31.center");
            var Q60;
            Q60=sQuery(id+"F2.wireOp",VERTEX,"E5.0.1.49.center");
            var Q61;
            Q61=sQuery(id+"F2.wireOp",VERTEX,"E4.0.0.41.center");
            var Q62;
            Q62=sQuery(id+"F2.wireOp",VERTEX,"E3.0.19.0.center");
            var Q63;
            Q63=sQuery(id+"F2.wireOp",VERTEX,"E4.0.0.42.center");
            var Q64;
            Q64=sQuery(id+"F2.wireOp",VERTEX,"E3.1.16.0.center");
            var Q65;
            Q65=sQuery(id+"F2.wireOp",VERTEX,"E3.1.7.0.center");
            var Q66;
            Q66=sQuery(id+"F2.wireOp",VERTEX,"E3.0.16.0.center");
            var Q67;
            Q67=sQuery(id+"F2.wireOp",VERTEX,"E3.1.6.0.center");
            var Q68;
            Q68=sQuery(id+"F2.wireOp",VERTEX,"E3.0.17.0.center");
            var Q69;
            Q69=sQuery(id+"F2.wireOp",VERTEX,"E3.1.15.0.center");
            var Q70;
            Q70=sQuery(id+"F2.wireOp",VERTEX,"E3.1.13.0.center");
            var Q71;
            Q71=sQuery(id+"F2.wireOp",VERTEX,"E3.0.15.0.center");
            var Q72;
            Q72=sQuery(id+"F2.wireOp",VERTEX,"E3.1.14.0.center");
            var Q73;
            Q73=sQuery(id+"F2.wireOp",VERTEX,"E3.0.11.0.center");
            var Q74;
            Q74=sQuery(id+"F2.wireOp",VERTEX,"E3.1.12.0.center");
            var Q75;
            Q75=sQuery(id+"F2.wireOp",VERTEX,"E3.1.11.0.center");
            var Q76;
            Q76=sQuery(id+"F2.wireOp",VERTEX,"E3.0.7.0.center");
            var Q77;
            Q77=sQuery(id+"F2.wireOp",VERTEX,"E3.1.3.0.center");
            var Q78;
            Q78=sQuery(id+"F2.wireOp",VERTEX,"E3.0.13.0.center");
            var Q79;
            Q79=sQuery(id+"F2.wireOp",VERTEX,"E3.0.12.0.center");
            var Q80;
            Q80=sQuery(id+"F2.wireOp",VERTEX,"E3.0.10.0.center");
            var Q81;
            Q81=sQuery(id+"F2.wireOp",VERTEX,"E3.1.9.0.center");
            var Q82;
            Q82=sQuery(id+"F2.wireOp",VERTEX,"E3.0.9.0.center");
            var Q83;
            Q83=sQuery(id+"F2.wireOp",VERTEX,"E3.1.2.0.center");
            var Q84;
            Q84=sQuery(id+"F2.wireOp",VERTEX,"E3.1.5.0.center");
            var Q85;
            Q85=sQuery(id+"F2.wireOp",VERTEX,"E3.1.17.0.center");
            var Q86;
            Q86=sQuery(id+"F2.wireOp",VERTEX,"E3.0.8.0.center");
            var Q87;
            Q87=sQuery(id+"F2.wireOp",VERTEX,"E3.0.6.0.center");
            var Q88;
            Q88=sQuery(id+"F2.wireOp",VERTEX,"E3.0.5.0.center");
            var Q89;
            Q89=sQuery(id+"F2.wireOp",VERTEX,"E3.0.4.0.center");
            var Q90;
            Q90=sQuery(id+"F2.wireOp",VERTEX,"E3.0.3.0.center");
            var Q91;
            Q91=sQuery(id+"F2.wireOp",VERTEX,"E3.0.2.0.center");
            var Q92;
            Q92=sQuery(id+"F2.wireOp",VERTEX,"E3.0.1.0.center");
            var Q93;
            Q93=sQuery(id+"F2.wireOp",VERTEX,"E2.center");
            var Q94;
            Q94=sQuery(id+"F2.wireOp",VERTEX,"E3.1.8.0.center");
            var Q95;
            Q95=sQuery(id+"F2.wireOp",VERTEX,"E3.1.1.0.center");
            var Q96;
            Q96=sQuery(id+"F2.wireOp",VERTEX,"E3.1.10.0.center");
            var Q97;
            Q97=sQuery(id+"F2.wireOp",VERTEX,"E3.direction1.end");
            var Q98;
            Q98=sQuery(id+"F2.wireOp",VERTEX,"E3.1.4.0.center");
            var Q99;
            Q99=sQuery(id+"F2.wireOp",VERTEX,"E3.0.14.0.center");
            var Q100;
            Q100=makeQuery(id+"F1.opExtrude","SWEPT_BODY",BODY,{"disambiguationData":[OSD([sQuery(id+"F0.wireOp",EDGE,"E0.bottom"),sQuery(id+"F0.wireOp",EDGE,"E0.top"),sQuery(id+"F0.wireOp",EDGE,"E0.left"),sQuery(id+"F0.wireOp",EDGE,"E0.right"),sQuery(id+"F0.wireOp",EDGE,"E1.bottom"),sQuery(id+"F0.wireOp",EDGE,"E1.top"),sQuery(id+"F0.wireOp",EDGE,"E1.left"),sQuery(id+"F0.wireOp",EDGE,"E1.right")])]});
            hole(context, id + "F5", {"style" : HoleStyle.SIMPLE, "endStyle" : HoleEndStyle.THROUGH, "holeDiameter" : 5.1 * mm, "isTappedThrough" : true, "tappedDepth" : 12.7 * mm, "tapClearance" : 3, "locations" : qUnion([Q0, Q1, Q2, Q3, Q4, Q5, Q6, Q7, Q8, Q9, Q10, Q11, Q12, Q13, Q14, Q15, Q16, Q17, Q18, Q19, Q20, Q21, Q22, Q23, Q24, Q25, Q26, Q27, Q28, Q29, Q30, Q31, Q32, Q33, Q34, Q35, Q36, Q37, Q38, Q39, Q40, Q41, Q42, Q43, Q44, Q45, Q46, Q47, Q48, Q49, Q50, Q51, Q52, Q53, Q54, Q55, Q56, Q57, Q58, Q59, Q60, Q61, Q62, Q63, Q64, Q65, Q66, Q67, Q68, Q69, Q70, Q71, Q72, Q73, Q74, Q75, Q76, Q77, Q78, Q79, Q80, Q81, Q82, Q83, Q84, Q85, Q86, Q87, Q88, Q89, Q90, Q91, Q92, Q93, Q94, Q95, Q96, Q97, Q98, Q99]), "scope" : qUnion([Q100])});
        }
        {
            var Q0;
            Q0=sQuery(id+"F2.wireOp",VERTEX,"E7.0.0.51.center");
            var Q1;
            Q1=sQuery(id+"F2.wireOp",VERTEX,"E7.0.1.51.center");
            var Q2;
            Q2=sQuery(id+"F2.wireOp",VERTEX,"E6.0.1.50.center");
            var Q3;
            Q3=sQuery(id+"F2.wireOp",VERTEX,"E6.0.0.50.center");
            var Q4;
            Q4=makeQuery(id+"F1.opExtrude","SWEPT_BODY",BODY,{"disambiguationData":[OSD([sQuery(id+"F0.wireOp",EDGE,"E0.bottom"),sQuery(id+"F0.wireOp",EDGE,"E0.top"),sQuery(id+"F0.wireOp",EDGE,"E0.left"),sQuery(id+"F0.wireOp",EDGE,"E0.right"),sQuery(id+"F0.wireOp",EDGE,"E1.bottom"),sQuery(id+"F0.wireOp",EDGE,"E1.top"),sQuery(id+"F0.wireOp",EDGE,"E1.left"),sQuery(id+"F0.wireOp",EDGE,"E1.right")])]});
            hole(context, id + "F6", {"style" : HoleStyle.SIMPLE, "endStyle" : HoleEndStyle.THROUGH, "holeDiameter" : 5.1 * mm, "isTappedThrough" : true, "tappedDepth" : 12.7 * mm, "tapClearance" : 3, "locations" : qUnion([Q0, Q1, Q2, Q3]), "scope" : qUnion([Q4])});
        }
    });
